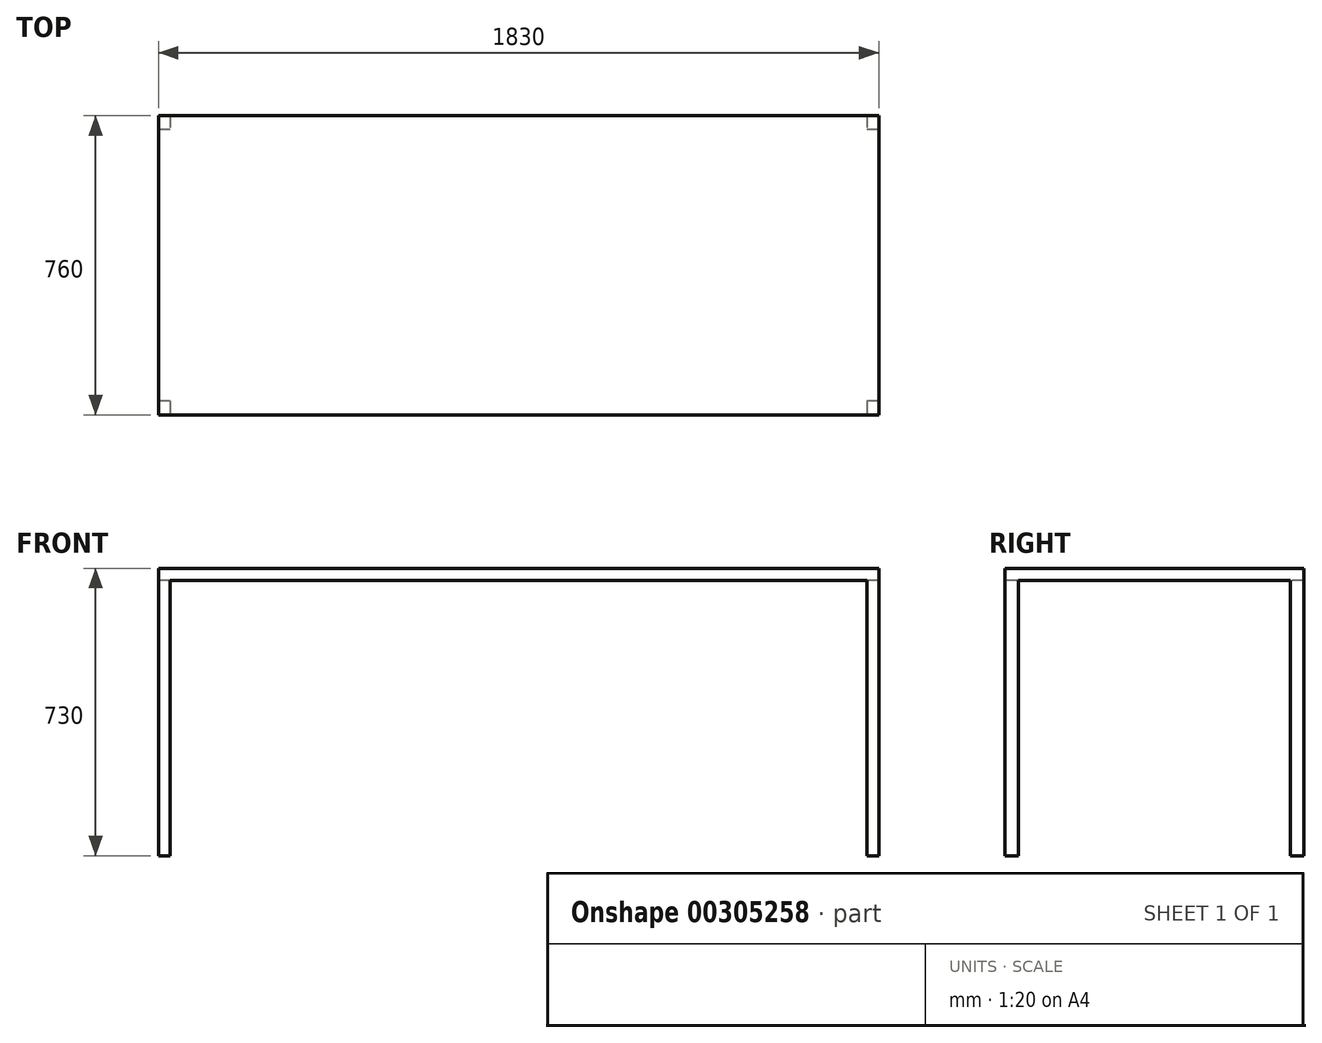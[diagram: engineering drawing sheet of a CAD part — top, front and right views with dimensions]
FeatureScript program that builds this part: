
annotation { "Feature Type Name" : "Feature", "Feature Type Description" : "" }
export const myFeature = defineFeature(function(context is Context, id is Id, definition is map)
    precondition{}
    {
        {
            var Q0;
            Q0=qCreatedBy(makeId("Top.planeOp"),FACE);
            var sketch = newSketch(context, id + "F0", { "sketchPlane" : qUnion([Q0])});
            skLineSegment(sketch, "E0.bottom", {"start": v(915, -380) * mm, "end": v(-915, -380) * mm});
            skLineSegment(sketch, "E0.top", {"start": v(915, 380) * mm, "end": v(-915, 380) * mm});
            skLineSegment(sketch, "E0.left", {"start": v(915, -380) * mm, "end": v(915, 380) * mm});
            skLineSegment(sketch, "E0.right", {"start": v(-915, -380) * mm, "end": v(-915, 380) * mm});
            skPoint(sketch, "E0.middle", {"position": v(0, 0) * mm});
            skSolve(sketch);
        }
        {
            var Q0;
            Q0 = qSketchRegion(id + "F0", true);
            extrude(context, id + "F1", {"entities" : qUnion([Q0]), "depth" : 730 * mm});
        }
        {
            var Q0;
            Q0=qCreatedBy(makeId("Top.planeOp"),FACE);
            var sketch = newSketch(context, id + "F2", { "sketchPlane" : qUnion([Q0])});
            skLineSegment(sketch, "E1.bottom", {"start": v(915, 345) * mm, "end": v(-915, 345) * mm});
            skLineSegment(sketch, "E1.top", {"start": v(915, -345) * mm, "end": v(-915, -345) * mm});
            skLineSegment(sketch, "E1.left", {"start": v(915, 345) * mm, "end": v(915, -345) * mm});
            skLineSegment(sketch, "E1.right", {"start": v(-915, 345) * mm, "end": v(-915, -345) * mm});
            skPoint(sketch, "E1.middle", {"position": v(0, 0) * mm});
            skLineSegment(sketch, "E2.bottom", {"start": v(885, 380) * mm, "end": v(-885, 380) * mm});
            skLineSegment(sketch, "E2.top", {"start": v(885, -380) * mm, "end": v(-885, -380) * mm});
            skLineSegment(sketch, "E2.left", {"start": v(885, 380) * mm, "end": v(885, -380) * mm});
            skLineSegment(sketch, "E2.right", {"start": v(-885, 380) * mm, "end": v(-885, -380) * mm});
            skSolve(sketch);
        }
        {
            var Q0;
            Q0 = qSketchRegion(id + "F2", true);
            extrude(context, id + "F3", {"entities" : qUnion([Q0]), "operationType" : NewBodyOperationType.REMOVE, "depth" : 700 * mm});
        }
    });
